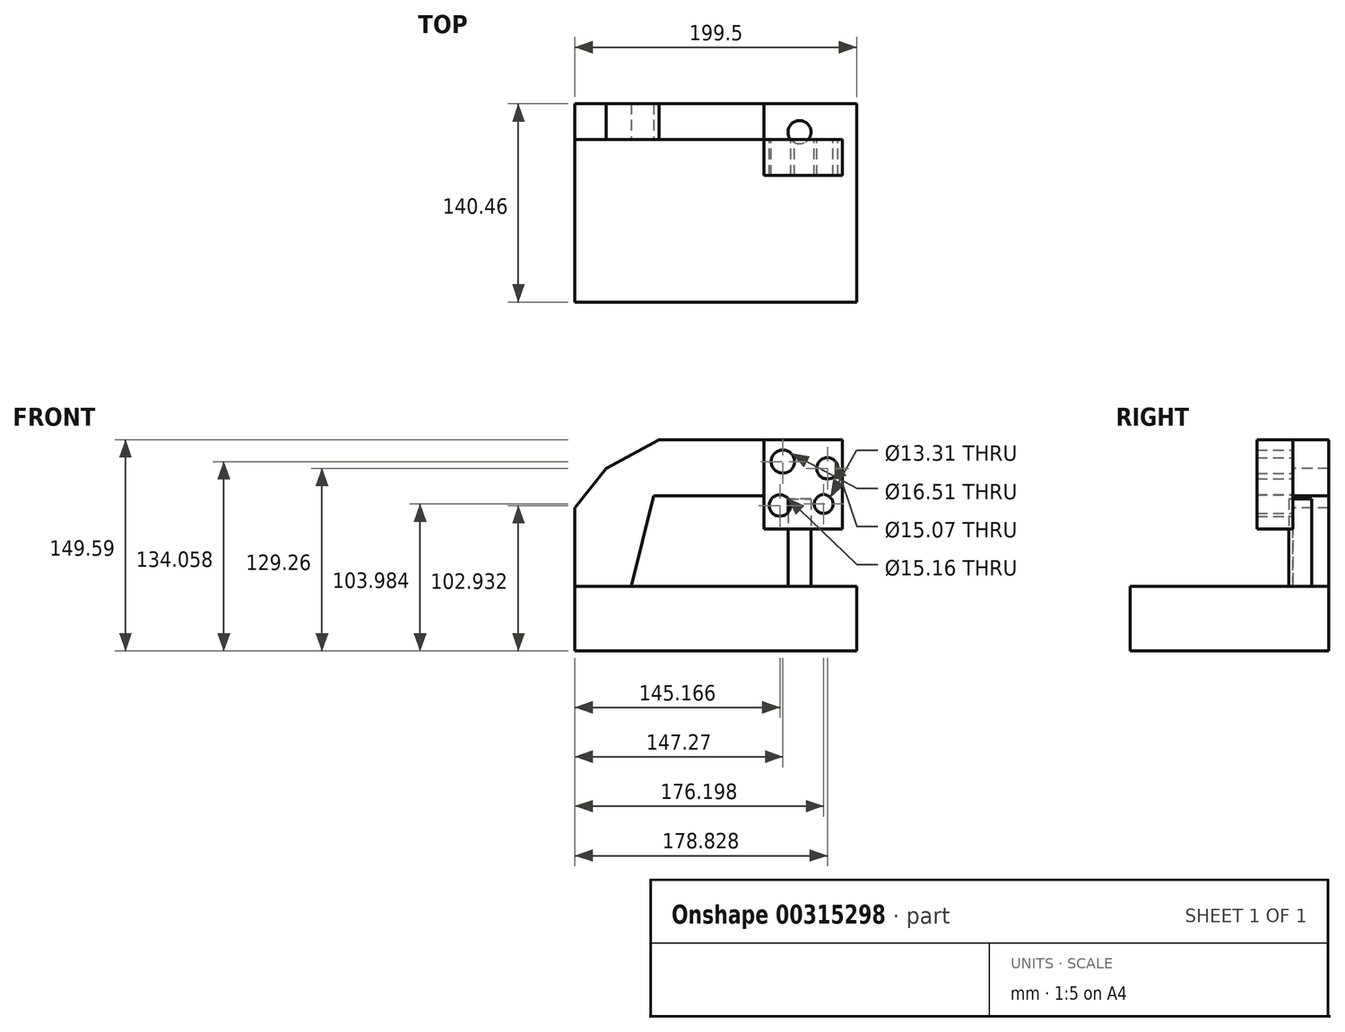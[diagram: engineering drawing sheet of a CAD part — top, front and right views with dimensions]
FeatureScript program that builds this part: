
annotation { "Feature Type Name" : "Feature", "Feature Type Description" : "" }
export const myFeature = defineFeature(function(context is Context, id is Id, definition is map)
    precondition{}
    {
        {
            var Q0;
            Q0=qCreatedBy(makeId("Front.planeOp"),FACE);
            var sketch = newSketch(context, id + "F0", { "sketchPlane" : qUnion([Q0])});
            skLineSegment(sketch, "E0.bottom", {"start": v(124.8, 20.33) * mm, "end": v(69.04, 20.33) * mm});
            skLineSegment(sketch, "E0.top", {"start": v(124.8, -42.78) * mm, "end": v(69.04, -42.78) * mm});
            skLineSegment(sketch, "E0.left", {"start": v(124.8, 20.33) * mm, "end": v(124.8, -42.78) * mm});
            skLineSegment(sketch, "E0.right", {"start": v(69.04, 20.33) * mm, "end": v(69.04, -42.78) * mm});
            skCircle(sketch, "E1", {"center": v(114.15, 0) * mm, "radius": 7.53 * mm});
            skCircle(sketch, "E2", {"center": v(82.59, 4.8) * mm, "radius": 8.26 * mm});
            skCircle(sketch, "E3", {"center": v(111.52, -25.28) * mm, "radius": 6.65 * mm});
            skCircle(sketch, "E4", {"center": v(80.49, -26.33) * mm, "radius": 7.58 * mm});
            skSolve(sketch);
        }
        {
            var Q0;
            Q0 = qSketchRegion(id + "F0", true);
            extrude(context, id + "F1", {"entities" : qUnion([Q0]), "depth" : 25.4 * mm});
        }
        {
            var Q0;
            Q0=makeQuery(id+"F1.opExtrude","CAP_FACE",FACE,{"disambiguationData":[OSD([sQuery(id+"F0.wireOp",EDGE,"E0.bottom"),sQuery(id+"F0.wireOp",EDGE,"E0.top"),sQuery(id+"F0.wireOp",EDGE,"E0.left"),sQuery(id+"F0.wireOp",EDGE,"E0.right"),sQuery(id+"F0.wireOp",EDGE,"E1"),sQuery(id+"F0.wireOp",EDGE,"E2"),sQuery(id+"F0.wireOp",EDGE,"E3"),sQuery(id+"F0.wireOp",EDGE,"E4")])],"isStart":true});
            var sketch = newSketch(context, id + "F2", { "sketchPlane" : qUnion([Q0])});
            skLineSegment(sketch, "E5", {"start": v(-69.04, 20.33) * mm, "end": v(5.25, 20.33) * mm});
            skLineSegment(sketch, "E6", {"start": v(5.25, 20.33) * mm, "end": v(42.6, 0) * mm});
            skLineSegment(sketch, "E7", {"start": v(42.6, 0) * mm, "end": v(64.68, -27.98) * mm});
            skLineSegment(sketch, "E8", {"start": v(64.68, -27.98) * mm, "end": v(64.68, -67.95) * mm});
            skLineSegment(sketch, "E9", {"start": v(64.68, -67.95) * mm, "end": v(64.68, -83.73) * mm});
            skLineSegment(sketch, "E10", {"start": v(64.68, -83.73) * mm, "end": v(24.7, -83.73) * mm});
            skLineSegment(sketch, "E11", {"start": v(24.7, -83.73) * mm, "end": v(8.93, -19.56) * mm});
            skLineSegment(sketch, "E12", {"start": v(8.93, -19.56) * mm, "end": v(-69.04, -19.56) * mm});
            skSolve(sketch);
        }
        {
            var Q0;
            {var subQ0=sQuery(id+"F2.wireOp",EDGE,"E5");Q0=makeQuery(id+"F2.imprint","IMPRINT",FACE,{"disambiguationData":[TD([[makeQuery(id+"F2.imprint","IMPRINT",EDGE,{"derivedFrom":subQ0}),-1.0]])]});}
            extrude(context, id + "F3", {"entities" : qUnion([Q0]), "depth" : 25.4 * mm});
        }
        {
            var Q0;
            Q0=makeQuery(id+"F3.opExtrude","CAP_FACE",FACE,{"disambiguationData":[OSD([sQuery(id+"F0.wireOp",EDGE,"E0.right"),sQuery(id+"F2.wireOp",EDGE,"E5"),sQuery(id+"F2.wireOp",EDGE,"E6"),sQuery(id+"F2.wireOp",EDGE,"E7"),sQuery(id+"F2.wireOp",EDGE,"E8"),sQuery(id+"F2.wireOp",EDGE,"E9"),sQuery(id+"F2.wireOp",EDGE,"E10"),sQuery(id+"F2.wireOp",EDGE,"E11"),sQuery(id+"F2.wireOp",EDGE,"E12")])],"isStart":false});
            var sketch = newSketch(context, id + "F4", { "sketchPlane" : qUnion([Q0])});
            skLineSegment(sketch, "E13.bottom", {"start": v(64.68, -83.73) * mm, "end": v(-134.82, -83.73) * mm});
            skLineSegment(sketch, "E13.top", {"start": v(64.68, -129.26) * mm, "end": v(-134.82, -129.26) * mm});
            skLineSegment(sketch, "E13.left", {"start": v(64.68, -83.73) * mm, "end": v(64.68, -129.26) * mm});
            skLineSegment(sketch, "E13.right", {"start": v(-134.82, -83.73) * mm, "end": v(-134.82, -129.26) * mm});
            skSolve(sketch);
        }
        {
            var Q0;
            Q0 = qSketchRegion(id + "F4", true);
            extrude(context, id + "F5", {"entities" : qUnion([Q0]), "operationType" : NewBodyOperationType.ADD, "oppositeDirection" : true, "depth" : 140.46 * mm});
        }
        {
            var Q0;
            Q0=makeQuery(id+"F5.opExtrude","SWEPT_FACE",FACE,{"disambiguationData":[OSD([sQuery(id+"F4.wireOp",EDGE,"E13.bottom")])]});
            var sketch = newSketch(context, id + "F6", { "sketchPlane" : qUnion([Q0])});
            skCircle(sketch, "E14", {"center": v(94.36, 5.3) * mm, "radius": 8.16 * mm});
            skSolve(sketch);
        }
        {
            var Q0;
            Q0 = qSketchRegion(id + "F6", true);
            extrude(context, id + "F7", {"entities" : qUnion([Q0]), "depth" : 61.98 * mm});
        }
    });
